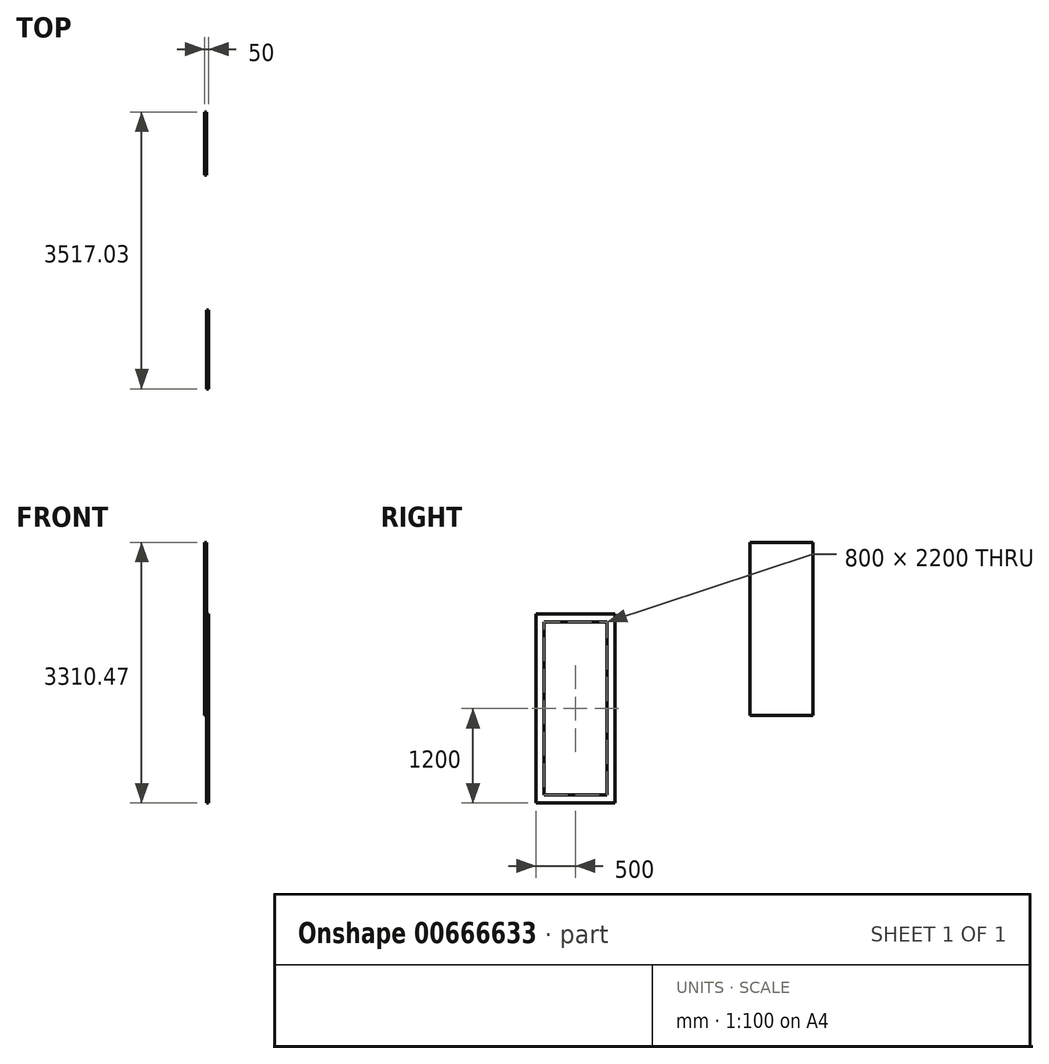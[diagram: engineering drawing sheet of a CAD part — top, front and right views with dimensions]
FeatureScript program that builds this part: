
annotation { "Feature Type Name" : "Feature", "Feature Type Description" : "" }
export const myFeature = defineFeature(function(context is Context, id is Id, definition is map)
    precondition{}
    {
        {
            var Q0;
            Q0=qCreatedBy(makeId("Right.planeOp"),FACE);
            var sketch = newSketch(context, id + "F0", { "sketchPlane" : qUnion([Q0])});
            skLineSegment(sketch, "E0.bottom", {"start": v(-500, -1200) * mm, "end": v(500, -1200) * mm});
            skLineSegment(sketch, "E0.top", {"start": v(-500, 1200) * mm, "end": v(500, 1200) * mm});
            skLineSegment(sketch, "E0.left", {"start": v(-500, -1200) * mm, "end": v(-500, 1200) * mm});
            skLineSegment(sketch, "E0.right", {"start": v(500, -1200) * mm, "end": v(500, 1200) * mm});
            skPoint(sketch, "E0.middle", {"position": v(0, 0) * mm});
            skLineSegment(sketch, "E1.bottom", {"start": v(-400, -1100) * mm, "end": v(400, -1100) * mm});
            skLineSegment(sketch, "E1.top", {"start": v(-400, 1100) * mm, "end": v(400, 1100) * mm});
            skLineSegment(sketch, "E1.left", {"start": v(-400, -1100) * mm, "end": v(-400, 1100) * mm});
            skLineSegment(sketch, "E1.right", {"start": v(400, -1100) * mm, "end": v(400, 1100) * mm});
            skSolve(sketch);
        }
        {
            var Q0;
            Q0=makeQuery(id+"F0.imprint","IMPRINT",FACE,{"disambiguationData":[TD([[makeQuery(id+"F0.imprint","IMPRINT",EDGE,{"derivedFrom":sQuery(id+"F0.wireOp",EDGE,"E0.bottom")}),1.0]])]});
            extrude(context, id + "F1", {"entities" : qUnion([Q0]), "depth" : 25 * mm, "offsetDistance" : 25 * mm});
        }
        {
            var Q0;
            Q0=makeQuery(id+"F1.opExtrude","CAP_FACE",FACE,{"disambiguationData":[OSD([sQuery(id+"F0.wireOp",EDGE,"E0.bottom"),sQuery(id+"F0.wireOp",EDGE,"E0.top"),sQuery(id+"F0.wireOp",EDGE,"E0.left"),sQuery(id+"F0.wireOp",EDGE,"E0.right"),sQuery(id+"F0.wireOp",EDGE,"E1.bottom"),sQuery(id+"F0.wireOp",EDGE,"E1.top"),sQuery(id+"F0.wireOp",EDGE,"E1.left"),sQuery(id+"F0.wireOp",EDGE,"E1.right")])],"isStart":true});
            var sketch = newSketch(context, id + "F2", { "sketchPlane" : qUnion([Q0])});
            skLineSegment(sketch, "E2.bottom", {"start": v(-2217.03, -89.53) * mm, "end": v(-3017.03, -89.53) * mm});
            skLineSegment(sketch, "E2.top", {"start": v(-2217.03, 2110.47) * mm, "end": v(-3017.03, 2110.47) * mm});
            skLineSegment(sketch, "E2.left", {"start": v(-2217.03, -89.53) * mm, "end": v(-2217.03, 2110.47) * mm});
            skLineSegment(sketch, "E2.right", {"start": v(-3017.03, -89.53) * mm, "end": v(-3017.03, 2110.47) * mm});
            skPoint(sketch, "E2.middle", {"position": v(-2617.03, 1010.47) * mm});
            skSolve(sketch);
        }
        {
            var Q0;
            Q0=makeQuery(id+"F2.imprint","IMPRINT",FACE,{"disambiguationData":[TD([[makeQuery(id+"F2.imprint","IMPRINT",EDGE,{"derivedFrom":sQuery(id+"F2.wireOp",EDGE,"E2.bottom")}),-1.0]])]});
            extrude(context, id + "F3", {"entities" : qUnion([Q0]), "depth" : 25 * mm, "offsetDistance" : 25 * mm});
        }
    });
